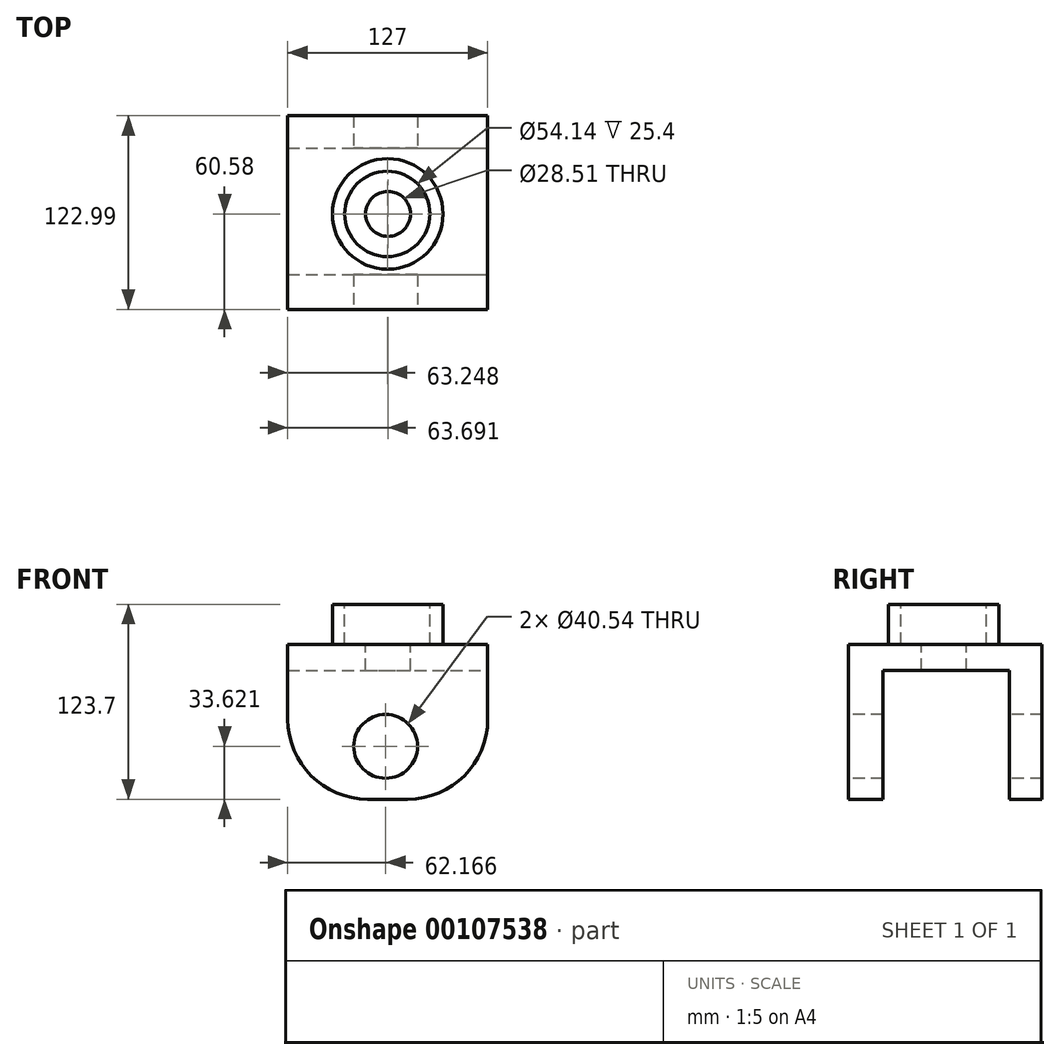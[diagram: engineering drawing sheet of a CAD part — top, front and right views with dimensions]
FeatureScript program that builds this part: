
annotation { "Feature Type Name" : "Feature", "Feature Type Description" : "" }
export const myFeature = defineFeature(function(context is Context, id is Id, definition is map)
    precondition{}
    {
        {
            var Q0;
            Q0=qCreatedBy(makeId("Right.planeOp"),FACE);
            var sketch = newSketch(context, id + "F0", { "sketchPlane" : qUnion([Q0])});
            skLineSegment(sketch, "E0.bottom", {"start": v(-60.58, 55.44) * mm, "end": v(62.4, 55.44) * mm});
            skLineSegment(sketch, "E0.top", {"start": v(-60.58, -42.86) * mm, "end": v(62.4, -42.86) * mm});
            skLineSegment(sketch, "E0.left", {"start": v(-60.58, 55.44) * mm, "end": v(-60.58, -42.86) * mm});
            skLineSegment(sketch, "E0.right", {"start": v(62.4, 55.44) * mm, "end": v(62.4, -42.86) * mm});
            skSolve(sketch);
        }
        {
            var Q0;
            Q0=makeQuery(id+"F0.imprint","IMPRINT",FACE,{"disambiguationData":[TD([[makeQuery(id+"F0.imprint","IMPRINT",EDGE,{"derivedFrom":sQuery(id+"F0.wireOp",EDGE,"E0.bottom")}),-1.0]])]});
            extrude(context, id + "F1", {"entities" : qUnion([Q0]), "depth" : 127 * mm});
        }
        {
            var Q0;
            Q0=makeQuery(id+"F1.opExtrude","CAP_FACE",FACE,{"disambiguationData":[OSD([sQuery(id+"F0.wireOp",EDGE,"E0.bottom"),sQuery(id+"F0.wireOp",EDGE,"E0.top"),sQuery(id+"F0.wireOp",EDGE,"E0.left"),sQuery(id+"F0.wireOp",EDGE,"E0.right")])],"isStart":false});
            var sketch = newSketch(context, id + "F2", { "sketchPlane" : qUnion([Q0])});
            skLineSegment(sketch, "E1.bottom", {"start": v(-38.63, 38.98) * mm, "end": v(41.83, 38.98) * mm});
            skLineSegment(sketch, "E1.top", {"start": v(-38.63, -42.86) * mm, "end": v(41.83, -42.86) * mm});
            skLineSegment(sketch, "E1.left", {"start": v(-38.63, 38.98) * mm, "end": v(-38.63, -42.86) * mm});
            skLineSegment(sketch, "E1.right", {"start": v(41.83, 38.98) * mm, "end": v(41.83, -42.86) * mm});
            skSolve(sketch);
        }
        {
            var Q0;
            Q0=makeQuery(id+"F2.imprint","IMPRINT",FACE,{"disambiguationData":[TD([[makeQuery(id+"F2.imprint","IMPRINT",EDGE,{"derivedFrom":sQuery(id+"F2.wireOp",EDGE,"E1.bottom")}),-1.0]])]});
            extrude(context, id + "F3", {"entities" : qUnion([Q0]), "operationType" : NewBodyOperationType.REMOVE, "oppositeDirection" : true, "depth" : 127 * mm});
        }
        {
            var Q0;
            {var subQ0=sQuery(id+"F0.wireOp",EDGE,"E0.left");var subQ1=sQuery(id+"F0.wireOp",EDGE,"E0.top");Q0=makeQuery(id+"F3.boolean.opBoolean","SPLIT",EDGE,{"disambiguationData":[TD([makeQuery(id+"F1.opExtrude","SWEPT_FACE",FACE,{"disambiguationData":[OSD([subQ0])]})])],"derivedFrom":makeQuery(id+"F1.opExtrude","CAP_EDGE",EDGE,{"disambiguationData":[OSD([subQ1])],"isStart":false})});}
            var Q1;
            {var subQ0=sQuery(id+"F0.wireOp",EDGE,"E0.left");var subQ1=sQuery(id+"F0.wireOp",EDGE,"E0.top");Q1=makeQuery(id+"F3.boolean.opBoolean","SPLIT",EDGE,{"disambiguationData":[TD([makeQuery(id+"F1.opExtrude","SWEPT_FACE",FACE,{"disambiguationData":[OSD([subQ0])]})])],"derivedFrom":makeQuery(id+"F1.opExtrude","CAP_EDGE",EDGE,{"disambiguationData":[OSD([subQ1])],"isStart":true})});}
            var Q2;
            {var subQ0=sQuery(id+"F0.wireOp",EDGE,"E0.right");var subQ1=sQuery(id+"F0.wireOp",EDGE,"E0.top");Q2=makeQuery(id+"F3.boolean.opBoolean","SPLIT",EDGE,{"disambiguationData":[TD([makeQuery(id+"F1.opExtrude","SWEPT_FACE",FACE,{"disambiguationData":[OSD([subQ0])]})])],"derivedFrom":makeQuery(id+"F1.opExtrude","CAP_EDGE",EDGE,{"disambiguationData":[OSD([subQ1])],"isStart":true})});}
            var Q3;
            {var subQ0=sQuery(id+"F0.wireOp",EDGE,"E0.right");var subQ1=sQuery(id+"F0.wireOp",EDGE,"E0.top");Q3=makeQuery(id+"F3.boolean.opBoolean","SPLIT",EDGE,{"disambiguationData":[TD([makeQuery(id+"F1.opExtrude","SWEPT_FACE",FACE,{"disambiguationData":[OSD([subQ0])]})])],"derivedFrom":makeQuery(id+"F1.opExtrude","CAP_EDGE",EDGE,{"disambiguationData":[OSD([subQ1])],"isStart":false})});}
            fillet(context, id + "F4", {"entities" : qUnion([Q0, Q1, Q2, Q3]), "radius" : 50.8 * mm, "tangentPropagation" : true, "allowEdgeOverflow" : false});
        }
        {
            var Q0;
            Q0=makeQuery(id+"F1.opExtrude","SWEPT_FACE",FACE,{"disambiguationData":[OSD([sQuery(id+"F0.wireOp",EDGE,"E0.left")])]});
            var sketch = newSketch(context, id + "F5", { "sketchPlane" : qUnion([Q0])});
            skCircle(sketch, "E2", {"center": v(62.17, -9.24) * mm, "radius": 20.27 * mm});
            skSolve(sketch);
        }
        {
            var Q0;
            Q0=makeQuery(id+"F5.imprint","IMPRINT",FACE,{"disambiguationData":[TD([[makeQuery(id+"F5.imprint","IMPRINT",EDGE,{"derivedFrom":sQuery(id+"F5.wireOp",EDGE,"E2")}),1.0]])]});
            extrude(context, id + "F6", {"entities" : qUnion([Q0]), "operationType" : NewBodyOperationType.REMOVE, "oppositeDirection" : true, "depth" : 254 * mm});
        }
        {
            var Q0;
            Q0=makeQuery(id+"F1.opExtrude","SWEPT_FACE",FACE,{"disambiguationData":[OSD([sQuery(id+"F0.wireOp",EDGE,"E0.bottom")])]});
            var sketch = newSketch(context, id + "F7", { "sketchPlane" : qUnion([Q0])});
            skCircle(sketch, "E3", {"center": v(63.5, 0) * mm, "radius": 35.13 * mm});
            skSolve(sketch);
        }
        {
            var Q0;
            Q0=makeQuery(id+"F7.imprint","IMPRINT",FACE,{"disambiguationData":[TD([[makeQuery(id+"F7.imprint","IMPRINT",EDGE,{"derivedFrom":sQuery(id+"F7.wireOp",EDGE,"E3")}),1.0]])]});
            extrude(context, id + "F8", {"entities" : qUnion([Q0]), "operationType" : NewBodyOperationType.ADD, "depth" : 25.4 * mm});
        }
        {
            var Q0;
            Q0=makeQuery(id+"F8.opExtrude","CAP_FACE",FACE,{"disambiguationData":[OSD([sQuery(id+"F7.wireOp",EDGE,"E3")])],"isStart":false});
            var sketch = newSketch(context, id + "F9", { "sketchPlane" : qUnion([Q0])});
            skSolve(sketch);
        }
        {
            var Q0;
            Q0=makeQuery(id+"F9.imprint","IMPRINT",FACE,{"disambiguationData":[TD([[makeQuery(id+"F9.imprint","IMPRINT",EDGE,{"derivedFrom":makeQuery(id+"F8.opExtrude","CAP_EDGE",EDGE,{"disambiguationData":[OSD([sQuery(id+"F7.wireOp",EDGE,"E3")])],"isStart":false})}),1.0]])]});
            var sketch = newSketch(context, id + "F10", { "sketchPlane" : qUnion([Q0])});
            skCircle(sketch, "E4", {"center": v(63.25, 0) * mm, "radius": 27.07 * mm});
            skSolve(sketch);
        }
        {
            var Q0;
            Q0=makeQuery(id+"F10.imprint","IMPRINT",FACE,{"disambiguationData":[TD([[makeQuery(id+"F10.imprint","IMPRINT",EDGE,{"derivedFrom":sQuery(id+"F10.wireOp",EDGE,"E4")}),1.0]])]});
            extrude(context, id + "F11", {"entities" : qUnion([Q0]), "operationType" : NewBodyOperationType.REMOVE, "oppositeDirection" : true, "depth" : 25.4 * mm});
        }
        {
            var Q0;
            Q0=makeQuery(id+"F9.imprint","IMPRINT",FACE,{"disambiguationData":[TD([[makeQuery(id+"F9.imprint","IMPRINT",EDGE,{"derivedFrom":makeQuery(id+"F8.opExtrude","CAP_EDGE",EDGE,{"disambiguationData":[OSD([sQuery(id+"F7.wireOp",EDGE,"E3")])],"isStart":false})}),1.0]])]});
            var sketch = newSketch(context, id + "F12", { "sketchPlane" : qUnion([Q0])});
            skCircle(sketch, "E5", {"center": v(63.7, 0) * mm, "radius": 14.26 * mm});
            skSolve(sketch);
        }
        {
            var Q0;
            Q0=makeQuery(id+"F12.imprint","IMPRINT",FACE,{"disambiguationData":[TD([[makeQuery(id+"F12.imprint","IMPRINT",EDGE,{"derivedFrom":sQuery(id+"F12.wireOp",EDGE,"E5")}),1.0]])]});
            extrude(context, id + "F13", {"entities" : qUnion([Q0]), "operationType" : NewBodyOperationType.REMOVE, "oppositeDirection" : true, "depth" : 50.8 * mm});
        }
    });
